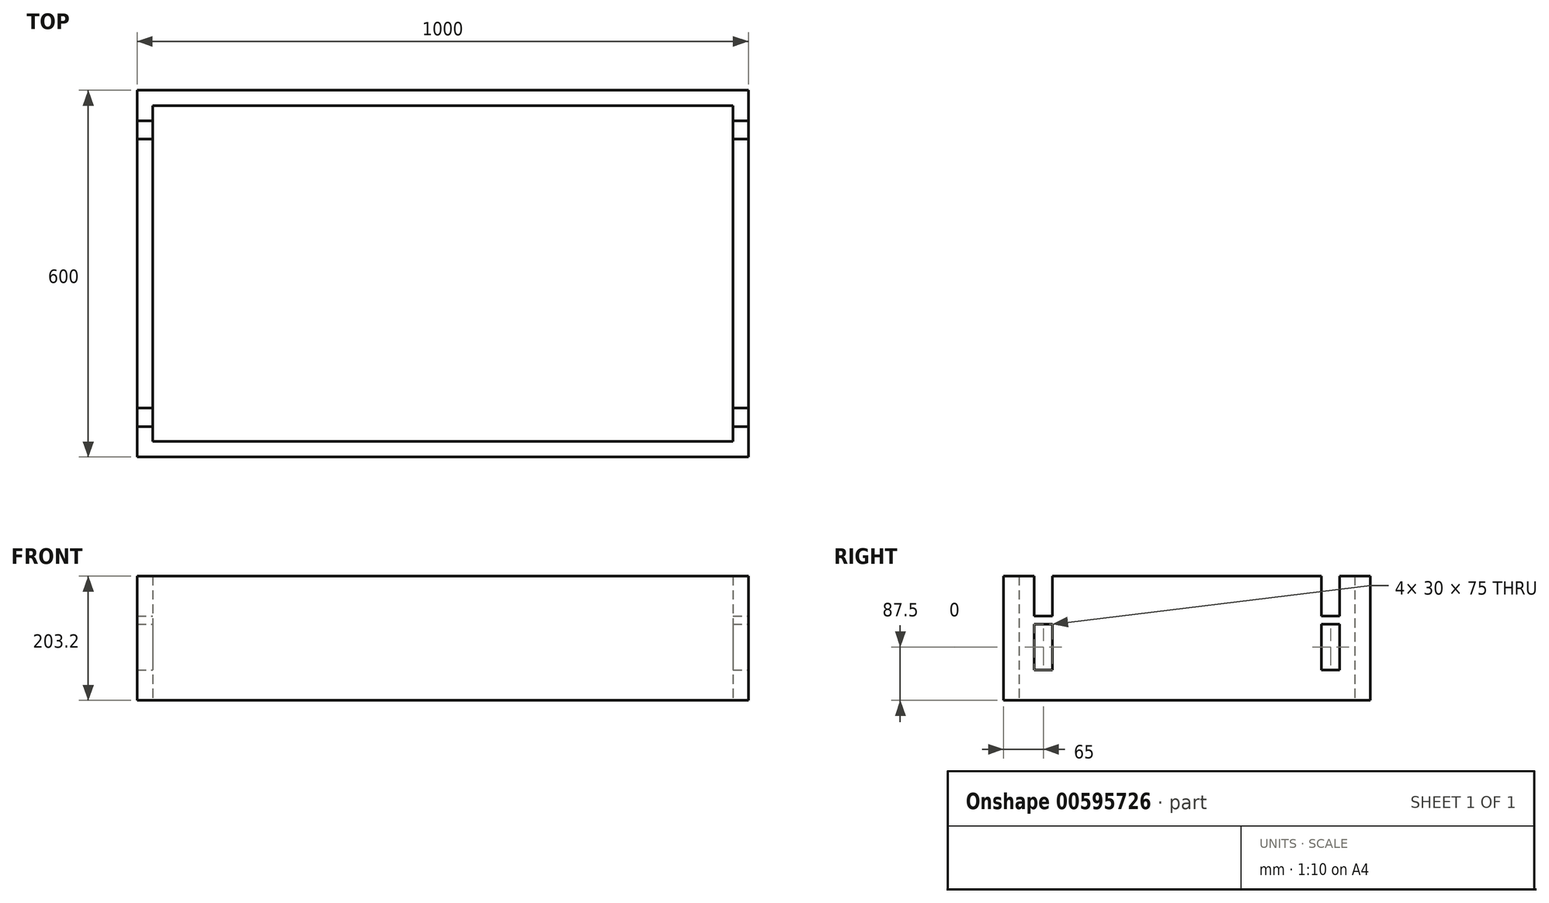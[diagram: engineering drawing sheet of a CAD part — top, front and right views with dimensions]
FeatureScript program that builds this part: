
annotation { "Feature Type Name" : "Feature", "Feature Type Description" : "" }
export const myFeature = defineFeature(function(context is Context, id is Id, definition is map)
    precondition{}
    {
        {
            var Q0;
            Q0=qCreatedBy(makeId("Top.planeOp"),FACE);
            var sketch = newSketch(context, id + "F0", { "sketchPlane" : qUnion([Q0])});
            skLineSegment(sketch, "E0.bottom", {"start": v(500, -300) * mm, "end": v(-500, -300) * mm});
            skLineSegment(sketch, "E0.top", {"start": v(500, 300) * mm, "end": v(-500, 300) * mm});
            skLineSegment(sketch, "E0.left", {"start": v(500, -300) * mm, "end": v(500, 300) * mm});
            skLineSegment(sketch, "E0.right", {"start": v(-500, -300) * mm, "end": v(-500, 300) * mm});
            skPoint(sketch, "E0.middle", {"position": v(0, 0) * mm});
            skLineSegment(sketch, "E1.bottom", {"start": v(-474.6, -274.6) * mm, "end": v(474.6, -274.6) * mm});
            skLineSegment(sketch, "E1.top", {"start": v(-474.6, 274.6) * mm, "end": v(474.6, 274.6) * mm});
            skLineSegment(sketch, "E1.left", {"start": v(-474.6, -274.6) * mm, "end": v(-474.6, 274.6) * mm});
            skLineSegment(sketch, "E1.right", {"start": v(474.6, -274.6) * mm, "end": v(474.6, 274.6) * mm});
            skSolve(sketch);
        }
        {
            var Q0;
            Q0=makeQuery(id+"F0.imprint","IMPRINT",FACE,{"disambiguationData":[TD([[makeQuery(id+"F0.imprint","IMPRINT",EDGE,{"derivedFrom":sQuery(id+"F0.wireOp",EDGE,"E0.bottom")}),-1.0]])]});
            extrude(context, id + "F1", {"entities" : qUnion([Q0]), "depth" : (8 * 25.4) * mm, "offsetDistance" : 25 * mm});
        }
        {
            var Q0;
            Q0=qCreatedBy(makeId("Right.planeOp"),FACE);
            var sketch = newSketch(context, id + "F2", { "sketchPlane" : qUnion([Q0])});
            skLineSegment(sketch, "E2.bottom", {"start": v(220, 138.2) * mm, "end": v(250, 138.2) * mm});
            skLineSegment(sketch, "E2.top", {"start": v(220, 213.2) * mm, "end": v(250, 213.2) * mm});
            skLineSegment(sketch, "E2.left", {"start": v(220, 138.2) * mm, "end": v(220, 213.2) * mm});
            skLineSegment(sketch, "E2.right", {"start": v(250, 138.2) * mm, "end": v(250, 213.2) * mm});
            skPoint(sketch, "E2.middle", {"position": v(235, 175.7) * mm});
            skLineSegment(sketch, "E3.bottom", {"start": v(-220, 138.2) * mm, "end": v(-250, 138.2) * mm});
            skLineSegment(sketch, "E3.top", {"start": v(-220, 213.2) * mm, "end": v(-250, 213.2) * mm});
            skLineSegment(sketch, "E3.left", {"start": v(-220, 138.2) * mm, "end": v(-220, 213.2) * mm});
            skLineSegment(sketch, "E3.right", {"start": v(-250, 138.2) * mm, "end": v(-250, 213.2) * mm});
            skPoint(sketch, "E3.middle", {"position": v(-235, 175.7) * mm});
            skLineSegment(sketch, "E4.bottom", {"start": v(-220, 50) * mm, "end": v(-250, 50) * mm});
            skLineSegment(sketch, "E4.top", {"start": v(-220, 125) * mm, "end": v(-250, 125) * mm});
            skLineSegment(sketch, "E4.left", {"start": v(-220, 50) * mm, "end": v(-220, 125) * mm});
            skLineSegment(sketch, "E4.right", {"start": v(-250, 50) * mm, "end": v(-250, 125) * mm});
            skPoint(sketch, "E4.middle", {"position": v(-235, 87.5) * mm});
            skLineSegment(sketch, "E5.bottom", {"start": v(250, 50) * mm, "end": v(220, 50) * mm});
            skLineSegment(sketch, "E5.top", {"start": v(250, 125) * mm, "end": v(220, 125) * mm});
            skLineSegment(sketch, "E5.left", {"start": v(250, 50) * mm, "end": v(250, 125) * mm});
            skLineSegment(sketch, "E5.right", {"start": v(220, 50) * mm, "end": v(220, 125) * mm});
            skPoint(sketch, "E5.middle", {"position": v(235, 87.5) * mm});
            skLineSegment(sketch, "E6", {"start": v(235, 175.7) * mm, "end": v(-235, 175.7) * mm, "construction": true});
            skLineSegment(sketch, "E7", {"start": v(235, 175.7) * mm, "end": v(235, 87.5) * mm, "construction": true});
            skLineSegment(sketch, "E8", {"start": v(-235, 175.7) * mm, "end": v(-235, 87.5) * mm, "construction": true});
            skLineSegment(sketch, "E9", {"start": v(235, 87.5) * mm, "end": v(-235, 87.5) * mm, "construction": true});
            skSolve(sketch);
        }
        {
            var Q0;
            Q0 = qSketchRegion(id + "F2", true);
            extrude(context, id + "F3", {"entities" : qUnion([Q0]), "operationType" : NewBodyOperationType.REMOVE, "endBound" : BoundingType.THROUGH_ALL, "oppositeDirection" : true, "depth" : 25 * mm, "offsetDistance" : 25 * mm, "hasSecondDirection" : true, "secondDirectionBound" : BoundingType.THROUGH_ALL, "secondDirectionOppositeDirection" : false, "secondDirectionDepth" : 25 * mm});
        }
    });
